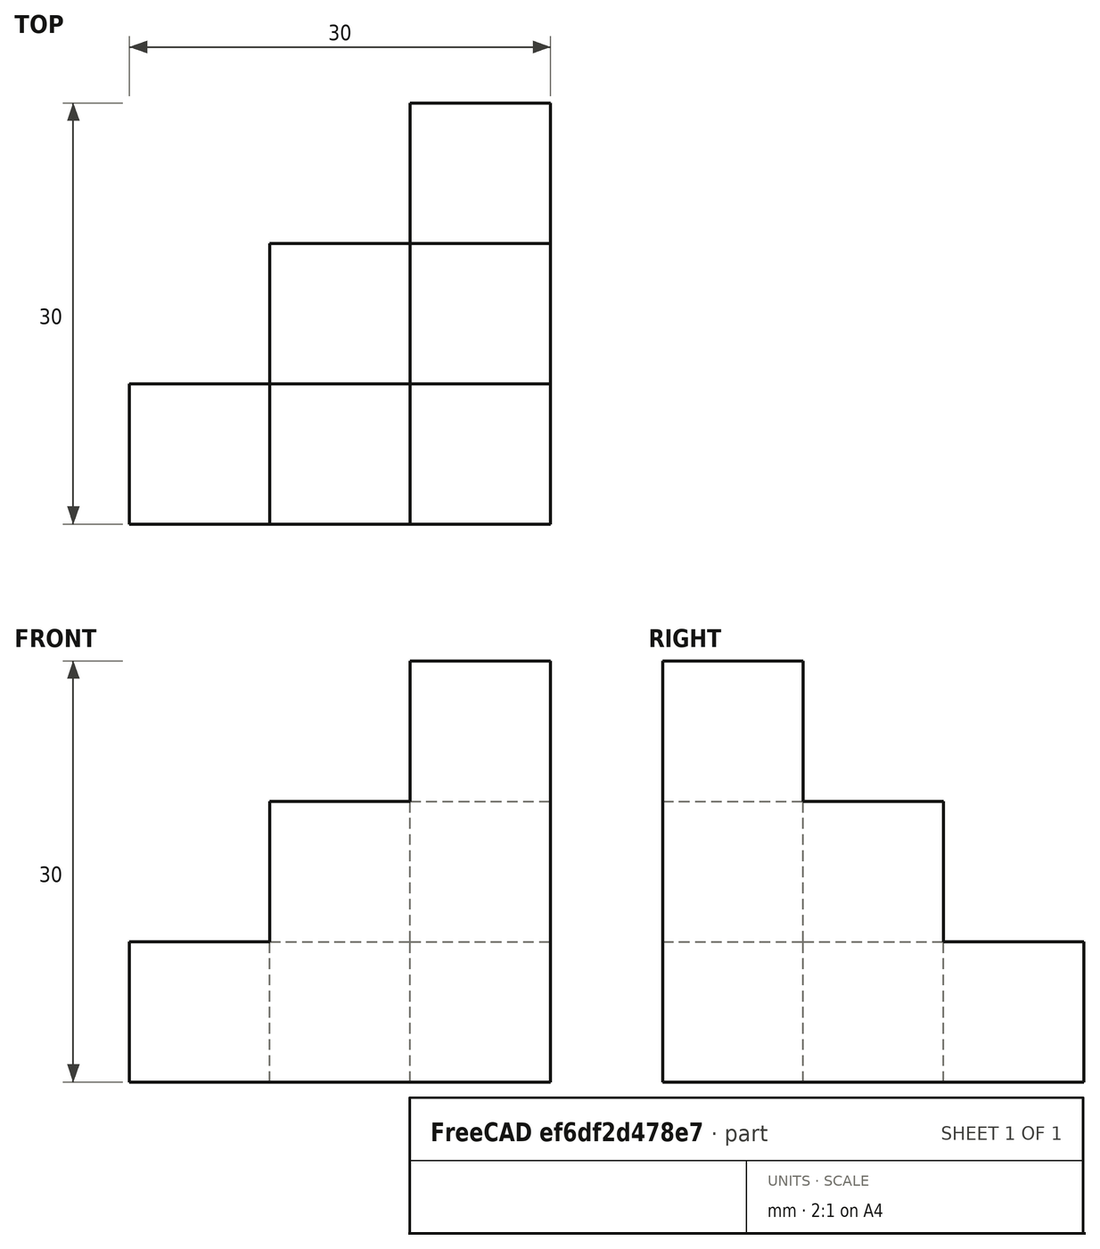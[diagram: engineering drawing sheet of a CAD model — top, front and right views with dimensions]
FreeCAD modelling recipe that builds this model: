
FCSTD DOCUMENT  (FreeCAD 0.21R33694 (Git))
Label: OJT1_T05R01_qubert4
License: All rights reserved
LicenseURL: https://en.wikipedia.org/wiki/All_rights_reserved
objects: Part::Box×6, Part::MultiFuse×1
note: 7 computed .brp shape members not serialized (recipe doc carries the construction recipe); baked Part::Feature solids carry a one-line shape summary decoded from their .brp

FEATURE [Part::Box] Box  label="Cub"
  AttacherType = Attacher::AttachEngine3D
  Height = 10
  Length = 10
  Placement = pos=(-10,0,0) rot=(0,0,1;0rad)
  Width = 10
FEATURE [Part::Box] Box003  label="Cub003"
  AttacherType = Attacher::AttachEngine3D
  Height = 20
  Length = 10
  Placement = pos=(10,10,0) rot=(0,0,1;0rad)
  Width = 10
FEATURE [Part::Box] Box005  label="Cub005"
  AttacherType = Attacher::AttachEngine3D
  Height = 30
  Length = 10
  Placement = pos=(10,0,0) rot=(0,0,1;0rad)
  Width = 10
FEATURE [Part::Box] Box007  label="Cub007"
  AttacherType = Attacher::AttachEngine3D
  Height = 20
  Length = 10
  Width = 10
FEATURE [Part::Box] Box008  label="Cub008"
  AttacherType = Attacher::AttachEngine3D
  Height = 10
  Length = 10
  Placement = pos=(0,10,0) rot=(0,0,1;0rad)
  Width = 10
FEATURE [Part::Box] Box009  label="Cub009"
  AttacherType = Attacher::AttachEngine3D
  Height = 10
  Length = 10
  Placement = pos=(10,20,0) rot=(0,0,1;0rad)
  Width = 10
FEATURE [Part::MultiFuse] Fusion
  Refine = true
  Shapes = -> [Box,Box003,Box005,Box007,Box008,Box009]
